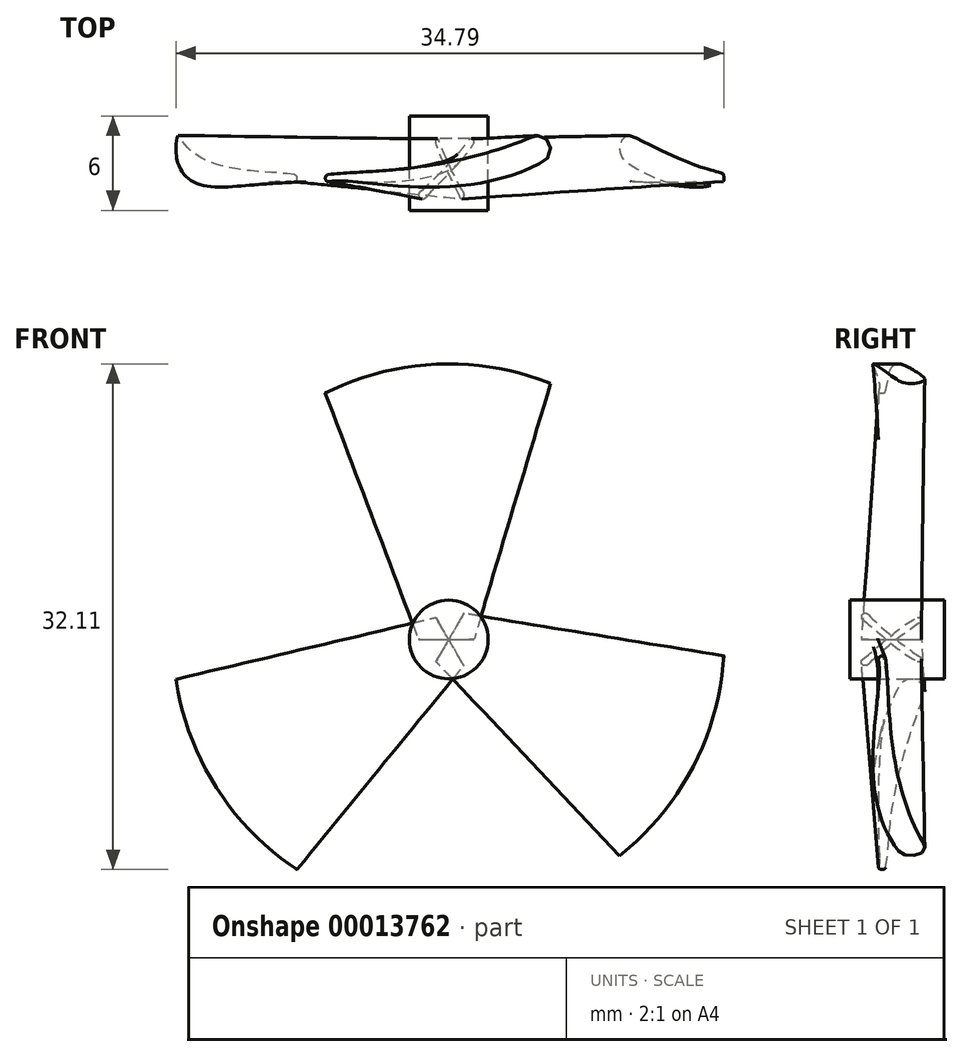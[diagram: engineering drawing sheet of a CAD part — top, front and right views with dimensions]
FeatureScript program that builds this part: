
annotation { "Feature Type Name" : "Feature", "Feature Type Description" : "" }
export const myFeature = defineFeature(function(context is Context, id is Id, definition is map)
    precondition{}
    {
        {
            var Q0;
            Q0=qCreatedBy(makeId("Front.planeOp"),FACE);
            var sketch = newSketch(context, id + "F0", { "sketchPlane" : qUnion([Q0])});
            skCircle(sketch, "E0", {"center": v(0, 0) * mm, "radius": 1.5 * mm});
            skCircle(sketch, "E1", {"center": v(0, 0) * mm, "radius": 2.5 * mm});
            skSolve(sketch);
        }
        {
            var Q0;
            Q0=qCreatedBy(makeId("Top.planeOp"),FACE);
            cPlane(context, id + "F1", {"entities" : qUnion([Q0]), "cplaneType" : CPlaneType.OFFSET, "offset" : 25 * mm, "width" : 150 * mm, "height" : 150 * mm});
        }
        {
            var Q0;
            Q0=makeQuery(id+"F0.imprint","IMPRINT",FACE,{"disambiguationData":[TD([[makeQuery(id+"F0.imprint","IMPRINT",EDGE,{"derivedFrom":sQuery(id+"F0.wireOp",EDGE,"E0")}),-1.0]])]});
            var Q1;
            Q1=makeQuery(id+"F0.imprint","IMPRINT",FACE,{"disambiguationData":[TD([[makeQuery(id+"F0.imprint","IMPRINT",EDGE,{"derivedFrom":sQuery(id+"F0.wireOp",EDGE,"E0")}),1.0]])]});
            extrude(context, id + "F2", {"entities" : qUnion([Q0, Q1]), "depth" : 3 * mm, "hasSecondDirection" : true, "secondDirectionOppositeDirection" : true, "secondDirectionDepth" : 3 * mm});
        }
        {
            var Q0;
            Q0=qCreatedBy(makeId("Top.planeOp"),FACE);
            var sketch = newSketch(context, id + "F3", { "sketchPlane" : qUnion([Q0])});
            skLineSegment(sketch, "E2", {"start": v(-1.46, -2.18) * mm, "end": v(-1.82, -1.81) * mm, "construction": true});
            skArc(sketch, "E3", {"start": v(-1.82, -1.81) * mm, "mid": v(-1.84, -2.2) * mm, "end": v(-1.46, -2.18) * mm});
            skFitSpline(sketch, "E4", {"points": [v(-1.46, -2.18) * mm, v(1.6, 1.29) * mm], "startDerivative": vector(2.25, 2.6) * mm, "endDerivative": vector(1.6, 3.07) * mm});
            skFitSpline(sketch, "E5", {"points": [v(-1.82, -1.81) * mm, v(1.29, 1.48) * mm], "startDerivative": vector(3.48, 2.91) * mm, "endDerivative": vector(1.93, 2.6) * mm});
            skArc(sketch, "E6", {"start": v(1.6, 1.29) * mm, "mid": v(1.53, 1.52) * mm, "end": v(1.29, 1.48) * mm});
            skLineSegment(sketch, "E7", {"start": v(0.97, 1.95) * mm, "end": v(1.7, 1.4) * mm, "construction": true});
            skLineSegment(sketch, "E8", {"start": v(1.7, 1.4) * mm, "end": v(-1.3, -2.6) * mm, "construction": true});
            skLineSegment(sketch, "E9", {"start": v(-1.3, -2.6) * mm, "end": v(-2.02, -2.06) * mm, "construction": true});
            skLineSegment(sketch, "E10", {"start": v(-2.02, -2.06) * mm, "end": v(0.97, 1.95) * mm, "construction": true});
            skLineSegment(sketch, "E11", {"start": v(0.97, 1.95) * mm, "end": v(-1.3, -2.6) * mm, "construction": true});
            skSolve(sketch);
        }
        {
            var Q0;
            Q0=qCreatedBy(id+"F1.planeOp",FACE);
            var sketch = newSketch(context, id + "F4", { "sketchPlane" : qUnion([Q0])});
            skLineSegment(sketch, "E12", {"start": v(9.31, 1.64) * mm, "end": v(8.2, -4.25) * mm, "construction": true});
            skLineSegment(sketch, "E13", {"start": v(8.2, -4.25) * mm, "end": v(-11.45, -0.53) * mm, "construction": true});
            skLineSegment(sketch, "E14", {"start": v(-11.45, -0.53) * mm, "end": v(-10.34, 5.37) * mm, "construction": true});
            skLineSegment(sketch, "E15", {"start": v(-10.34, 5.37) * mm, "end": v(9.31, 1.64) * mm, "construction": true});
            skArc(sketch, "E16", {"start": v(8.35, -0.5) * mm, "mid": v(9.02, 1.1) * mm, "end": v(7.45, 1.82) * mm});
            skArc(sketch, "E17", {"start": v(-11.13, -0.09) * mm, "mid": v(-11.4, -0.3) * mm, "end": v(-11.2, -0.58) * mm});
            skFitSpline(sketch, "E18", {"points": [v(8.35, -0.5) * mm, v(-11.2, -0.58) * mm], "startDerivative": vector(-25.51, -10.83) * mm, "endDerivative": vector(-8.06, 1.18) * mm});
            skFitSpline(sketch, "E19", {"points": [v(7.45, 1.82) * mm, v(-11.13, -0.09) * mm], "startDerivative": vector(-25.8, -9.04) * mm, "endDerivative": vector(-12, 1.68) * mm});
            skLineSegment(sketch, "E20", {"start": v(8.2, -4.25) * mm, "end": v(-10.34, 5.37) * mm, "construction": true});
            skLineSegment(sketch, "E21", {"start": v(-11.13, -0.09) * mm, "end": v(-11.2, -0.58) * mm, "construction": true});
            skLineSegment(sketch, "E22", {"start": v(8.35, -0.5) * mm, "end": v(7.45, 1.82) * mm, "construction": true});
            skSolve(sketch);
        }
        {
            var Q1;
            Q1 = qSketchRegion(id + "F3", true);
            var Q2;
            Q2 = qSketchRegion(id + "F4", true);
            loft(context, id + "F5", {"sheetProfilesArray" : [{ "sheetProfileEntities" : qUnion([Q1]) }, { "sheetProfileEntities" : qUnion([Q2]) }]});
        }
        {
            var Q0;
            Q0=makeQuery(id+"F5.opLoft","SWEPT_BODY",BODY,{"disambiguationData":[OSD([makeQuery(id+"F3.imprint","IMPRINT",FACE,{"disambiguationData":[TD([[makeQuery(id+"F3.imprint","IMPRINT",EDGE,{"derivedFrom":sQuery(id+"F3.wireOp",EDGE,"E3")}),1.0]])]}),makeQuery(id+"F4.imprint","IMPRINT",FACE,{"disambiguationData":[TD([[makeQuery(id+"F4.imprint","IMPRINT",EDGE,{"derivedFrom":sQuery(id+"F4.wireOp",EDGE,"E16")}),1.0]])]})])]});
            var Q1;
            Q1=sQuery(id+"F0.wireOp",EDGE,"E1");
            circularPattern(context, id + "F6", {"entities" : qUnion([Q0]), "axis" : qUnion([Q1]), "angle" : 120 * degree, "instanceCount" : 3});
        }
        {
            var Q0;
            Q0=qCreatedBy(makeId("Front.planeOp"),FACE);
            var sketch = newSketch(context, id + "F7", { "sketchPlane" : qUnion([Q0])});
            skCircle(sketch, "E23", {"center": v(0, 0) * mm, "radius": 17.5 * mm});
            skCircle(sketch, "E24", {"center": v(0, 0) * mm, "radius": 28.77 * mm});
            skSolve(sketch);
        }
        {
            var Q0;
            Q0 = qSketchRegion(id + "F7", true);
            extrude(context, id + "F8", {"entities" : qUnion([Q0]), "operationType" : NewBodyOperationType.REMOVE, "endBound" : BoundingType.THROUGH_ALL, "depth" : 25 * mm, "hasSecondDirection" : true, "secondDirectionBound" : SecondDirectionBoundingType.THROUGH_ALL, "secondDirectionOppositeDirection" : true, "secondDirectionDepth" : 25 * mm});
        }
    });
